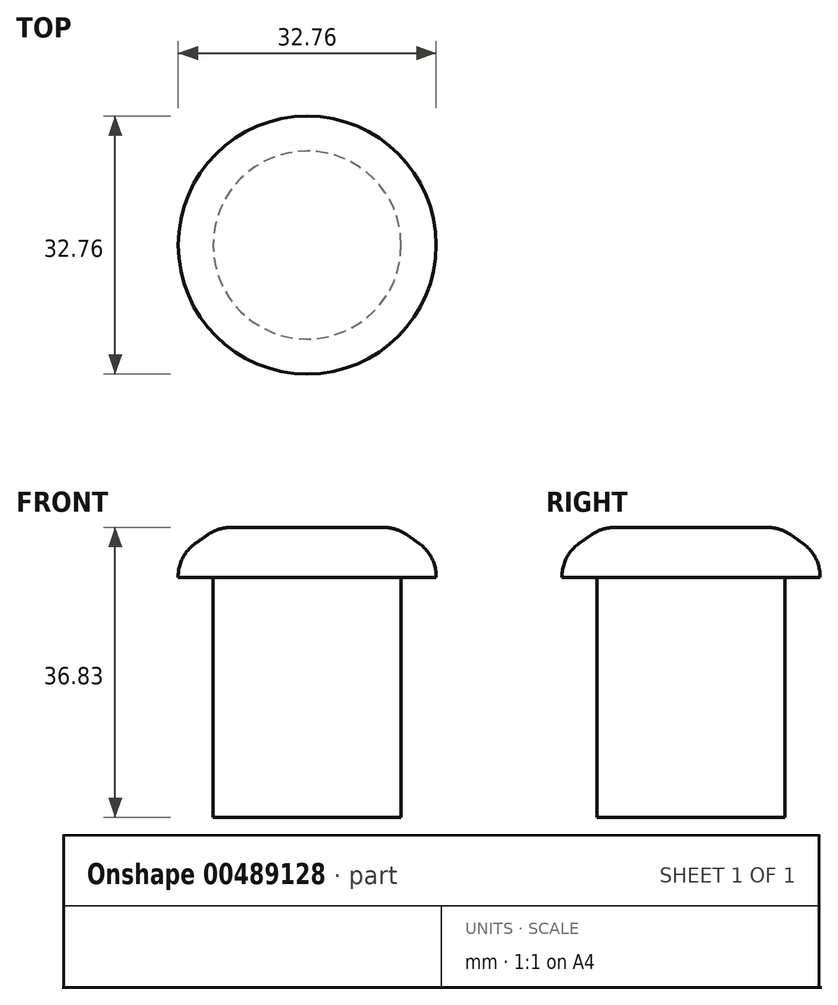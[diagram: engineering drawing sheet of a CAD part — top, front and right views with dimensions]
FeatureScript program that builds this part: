
annotation { "Feature Type Name" : "Feature", "Feature Type Description" : "" }
export const myFeature = defineFeature(function(context is Context, id is Id, definition is map)
    precondition{}
    {
        {
            var Q0;
            Q0=qCreatedBy(makeId("Top.planeOp"),FACE);
            var sketch = newSketch(context, id + "F0", { "sketchPlane" : qUnion([Q0])});
            skCircle(sketch, "E0", {"center": v(0, 0) * mm, "radius": 11.94 * mm});
            skSolve(sketch);
        }
        {
            var Q0;
            Q0=makeQuery(id+"F0.imprint","IMPRINT",FACE,{"disambiguationData":[TD([[makeQuery(id+"F0.imprint","IMPRINT",EDGE,{"derivedFrom":sQuery(id+"F0.wireOp",EDGE,"E0")}),1.0]])]});
            extrude(context, id + "F1", {"entities" : qUnion([Q0]), "depth" : 30.48 * mm});
        }
        {
            var Q0;
            Q0=makeQuery(id+"F1.opExtrude","CAP_FACE",FACE,{"disambiguationData":[OSD([sQuery(id+"F0.wireOp",EDGE,"E0")])],"isStart":false});
            var sketch = newSketch(context, id + "F2", { "sketchPlane" : qUnion([Q0])});
            skCircle(sketch, "E1", {"center": v(0, 0) * mm, "radius": 16.38 * mm});
            skSolve(sketch);
        }
        {
            var Q0;
            Q0=makeQuery(id+"F2.imprint","IMPRINT",FACE,{"disambiguationData":[TD([[makeQuery(id+"F2.imprint","IMPRINT",EDGE,{"derivedFrom":sQuery(id+"F2.wireOp",EDGE,"E1")}),1.0]])]});
            var Q1;
            Q1=makeQuery(id+"F2.imprint","IMPRINT",FACE,{"disambiguationData":[TD([[makeQuery(id+"F2.imprint","IMPRINT",EDGE,{"derivedFrom":makeQuery(id+"F1.opExtrude","CAP_EDGE",EDGE,{"disambiguationData":[OSD([sQuery(id+"F0.wireOp",EDGE,"E0")])],"isStart":false})}),1.0]])]});
            extrude(context, id + "F3", {"entities" : qUnion([Q0, Q1]), "operationType" : NewBodyOperationType.ADD, "depth" : 6.35 * mm});
        }
        {
            var Q0;
            Q0=makeQuery(id+"F3.opExtrude","CAP_EDGE",EDGE,{"disambiguationData":[OSD([sQuery(id+"F2.wireOp",EDGE,"E1")])],"isStart":false});
            chamfer(context, id + "F4", {"entities" : qUnion([Q0]), "chamferType" : ChamferType.OFFSET_ANGLE, "width" : 5.08 * mm, "oppositeDirection" : false, "angle" : 35 * degree, "tangentPropagation" : true});
        }
        {
            var Q0;
            {var subQ0=sQuery(id+"F2.wireOp",EDGE,"E1");Q0=makeQuery(id+"F4.opChamfer","BLEND_EDGE",EDGE,{"blendedFrom":[makeQuery(id+"F3.opExtrude","CAP_EDGE",EDGE,{"disambiguationData":[OSD([subQ0])],"isStart":false}),makeQuery(id+"F3.opExtrude","CAP_FACE",FACE,{"disambiguationData":[OSD([subQ0])],"isStart":false})],"blendedInto":[makeQuery(id+"F3.opExtrude","CAP_FACE",FACE,{"disambiguationData":[OSD([subQ0])],"isStart":false})]});}
            var Q1;
            {var subQ0=sQuery(id+"F2.wireOp",EDGE,"E1");Q1=makeQuery(id+"F4.opChamfer","BLEND_EDGE",EDGE,{"blendedFrom":[makeQuery(id+"F3.opExtrude","CAP_EDGE",EDGE,{"disambiguationData":[OSD([subQ0])],"isStart":false}),makeQuery(id+"F3.opExtrude","SWEPT_FACE",FACE,{"disambiguationData":[OSD([subQ0])]})],"blendedInto":[makeQuery(id+"F3.opExtrude","SWEPT_FACE",FACE,{"disambiguationData":[OSD([subQ0])]})]});}
            fillet(context, id + "F5", {"entities" : qUnion([Q0, Q1]), "radius" : 5.08 * mm, "tangentPropagation" : true, "allowEdgeOverflow" : false});
        }
    });
